# Revit family: IS_Joy_BC782_BIM_GB
name_source: partatom
category: Plumbing Fixtures
revit_build: Autodesk Revit 2017 (Build: 20160225_1515(x64)
units: mm (PartAtom-declared; Revit-internal decimal feet)

## family parameters
Always vertical = No
Cut with Voids When Loaded = No
OmniClass Number = 23.45.55.17
OmniClass Title = Mixing Faucets
Part Type = Normal
Room Calculation Point = No
Round Connector Dimension = Use Diameter
Shared = No
Work Plane-Based = No

## types (4) — shared parameters
Accessories = https://www.idealstandard.co.uk
AssetType = Fixed
BIMObjectName = ISI_IdealStandard_Washbasin manual water supply sets_Joy_BC782
BarCode = 3800861086871
Brand = Ideal Standard
CurrencyUnit = £
Description = JOY Single lever basin mixer JOY, with extended base. 170mm spout projection. Available in four different finishes, Chrome (AA), Silver storm (GN) 386, Brushed gold (A2) and Magnetic grey (A5)
DistributedBy = Ideal Standard
DurationUnit = Years
ExpectedLife = 30
FaucetFunction = MIXED
FaucetOperation = OTHER
FaucetType = OTHER
Features = Single lever basin mixer JOY, with extended base. 170mm spout projection. Available in four different finishes, Chrome (AA), Silver storm (GN) 386, Brushed gold (A2) and Magnetic grey (A5)
Help = https://www.idealstandard.co.uk
IfcExportAs = IfcValveType
IfcExportType = FAUCET
Installation instructions = https://www.idealspec.co.uk
InstallationInstructions = https://www.idealstandard.co.uk
IsBuiltIn = No
MaintenanceInformation = https://www.idealstandard.co.uk
Manufacturer = Ideal Standard
ManufacturerURL = https://www.idealstandard.co.uk
Material = Brass
ModelNumber = BC782
NBS Reference Code = 45-35-70/371
NBS Reference Description = Water supply fittings for wash basins and troughs
Name = Washbasin manual water supply sets_Joy_BC782_IdealStandard
NettWeight = 1.95
NominalHeight = 75 mm
Product certification = https://www.idealstandard.co.uk
Product group = BASIN MIXER
ProductInformation = https://www.idealspec.co.uk
Shape = Sculptured
Size = 48 x 203 x 313 mm
Space = Internal
SpareParts = https://www.idealspec.co.uk
SustainabilityPerformance = https://www.idealspec.co.uk
TestPressure = 10 Bar
URL = https://www.idealstandard.co.uk
Uniclass 2015 Code = Pr_40_20_87_96
Uniclass 2015 Name = Washbasin manual water supply sets
Uniclass2015Code = Pr_40_20_87_96
Uniclass2015Title = Washbasin manual water supply sets
Uniclass2015Version = v1.1
Version = 1
VolumeUnits = Litres
WRASURL = https://www.wras.co.uk
WarrantyDescription = Manufacturers Warranty
WarrantyDurationParts = 5
WarrantyDurationUnit = year
WarrantyGuarantorParts = https://www.idealspec.co.uk
WorkingPressure = 3bar
zero-valued in all types: InletConnectionSize, MaterialThickness, NominalDepth, NominalLength, NominalWidth

## per-type parameters (varying)
| type | Color | Finish | MainColor | Model | ModelReference |
| BC782A2 - JOY VSL MXR RMTD 5L NO PUW BR GOLD | Brushed Gold | Brushed Gold | Brushed Gold | BC782A2 | BC782A2 |
| BC782A5 - JOY VSL MXR RMTD 5L NO PUW MGN GREY | Magnetic grey | Magnetic grey | Magnetic grey | BC782A5 | BC782A5 |
| BC782AA - JOY VSL MXR RMTD 5L NO PUW CHR | Chrome | Chrome | Chrome | BC782AA | BC782AA |
| BC782GN - JOY VSL MXR RMTD 5L NO PUW SILV STORM | Silver storm | Silver storm | Silver storm | BC782GN | BC782GN |

## geometry (parser evidence)
native form markers: Sweep x3
no freeform markers — native parametric forms only
